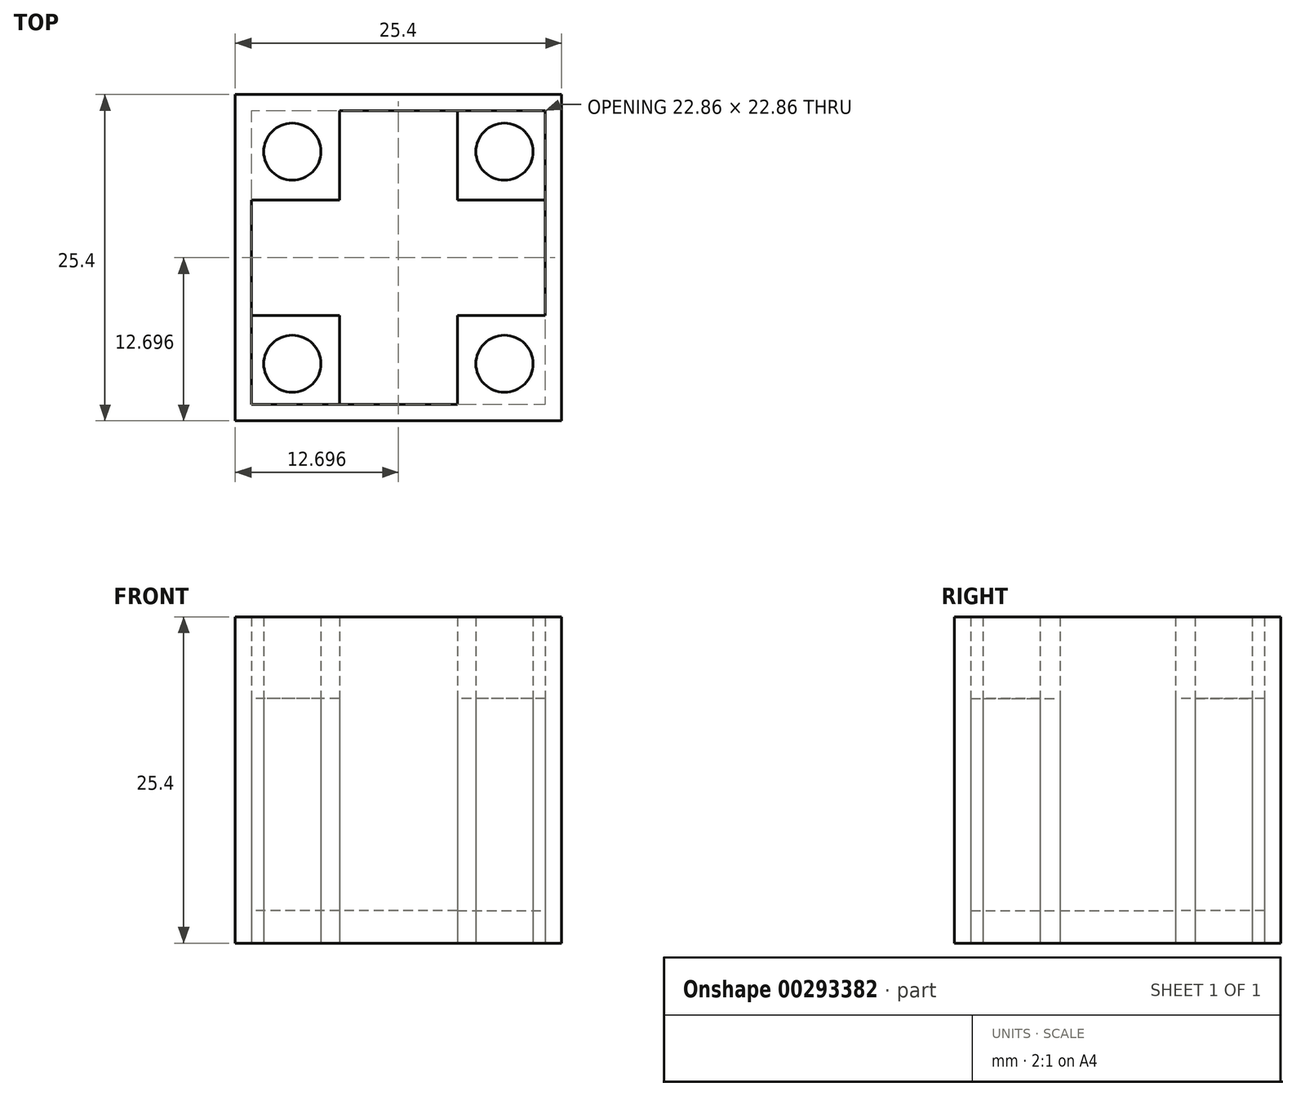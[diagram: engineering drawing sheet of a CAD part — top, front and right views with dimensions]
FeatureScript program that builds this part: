
annotation { "Feature Type Name" : "Feature", "Feature Type Description" : "" }
export const myFeature = defineFeature(function(context is Context, id is Id, definition is map)
    precondition{}
    {
        {
            var Q0;
            Q0=qCreatedBy(makeId("Top.planeOp"),FACE);
            var sketch = newSketch(context, id + "F0", { "sketchPlane" : qUnion([Q0])});
            skLineSegment(sketch, "E0.bottom", {"start": v(-7.95, 16.08) * mm, "end": v(17.45, 16.08) * mm});
            skLineSegment(sketch, "E0.top", {"start": v(-7.95, -9.32) * mm, "end": v(17.45, -9.32) * mm});
            skLineSegment(sketch, "E0.left", {"start": v(-7.95, 16.08) * mm, "end": v(-7.95, -9.32) * mm});
            skLineSegment(sketch, "E0.right", {"start": v(17.45, 16.08) * mm, "end": v(17.45, -9.32) * mm});
            skLineSegment(sketch, "E1", {"start": v(16.18, 14.8) * mm, "end": v(16.18, -8.05) * mm});
            skLineSegment(sketch, "E2", {"start": v(16.18, -8.05) * mm, "end": v(-6.68, -8.05) * mm});
            skLineSegment(sketch, "E3", {"start": v(-6.68, -8.05) * mm, "end": v(-6.68, 14.8) * mm});
            skLineSegment(sketch, "E4", {"start": v(-6.68, 14.8) * mm, "end": v(-4.14, 14.8) * mm});
            skLineSegment(sketch, "E5", {"start": v(-6.68, -8.05) * mm, "end": v(-4.14, -8.05) * mm});
            skLineSegment(sketch, "E6", {"start": v(16.18, 14.8) * mm, "end": v(13.64, 14.8) * mm});
            skPoint(sketch, "E7.endSnap0", {"position": v(4.75, -9.32) * mm});
            skLineSegment(sketch, "E8", {"start": v(-6.68, 14.8) * mm, "end": v(16.18, 14.8) * mm});
            skPoint(sketch, "E9.endSnap0", {"position": v(4.75, -8.05) * mm});
            skLineSegment(sketch, "E10", {"start": v(0.16, 14.8) * mm, "end": v(0.16, 7.86) * mm});
            skLineSegment(sketch, "E11", {"start": v(0.16, 7.86) * mm, "end": v(-6.68, 7.86) * mm});
            skCircle(sketch, "E12", {"center": v(-3.5, 11.63) * mm, "radius": 2.22 * mm});
            skCircle(sketch, "E13.MirrorC", {"center": v(13, 11.63) * mm, "radius": 2.22 * mm});
            skCircle(sketch, "E14.MirrorC", {"center": v(13, -4.88) * mm, "radius": 2.22 * mm});
            skCircle(sketch, "E15.MirrorC", {"center": v(-3.5, -4.88) * mm, "radius": 2.22 * mm});
            skPoint(sketch, "E16.endSnap0", {"position": v(-6.68, 3.38) * mm});
            skLineSegment(sketch, "E17.MirrorCS", {"start": v(9.34, 7.86) * mm, "end": v(16.18, 7.86) * mm});
            skLineSegment(sketch, "E18.MirrorCS", {"start": v(9.34, 14.8) * mm, "end": v(9.34, 7.86) * mm});
            skLineSegment(sketch, "E19.MirrorCS", {"start": v(9.34, -1.11) * mm, "end": v(16.18, -1.11) * mm});
            skLineSegment(sketch, "E20.MirrorCS", {"start": v(9.34, -8.05) * mm, "end": v(9.34, -1.11) * mm});
            skLineSegment(sketch, "E21.MirrorCS", {"start": v(0.16, -8.05) * mm, "end": v(0.16, -1.11) * mm});
            skLineSegment(sketch, "E22.MirrorCS", {"start": v(0.16, -1.11) * mm, "end": v(-6.68, -1.11) * mm});
            skSolve(sketch);
        }
        {
            var Q0;
            {var subQ6=sQuery(id+"F0.wireOp",EDGE,"E10");Q0=makeQuery(id+"F0.imprint","IMPRINT",FACE,{"disambiguationData":[TD([[makeQuery(id+"F0.imprint","IMPRINT",EDGE,{"derivedFrom":subQ6}),1.0]])]});}
            extrude(context, id + "F1", {"entities" : qUnion([Q0]), "depth" : 2.54 * mm});
        }
        {
            var Q0;
            Q0=makeQuery(id+"F0.imprint","IMPRINT",FACE,{"disambiguationData":[TD([[makeQuery(id+"F0.imprint","IMPRINT",EDGE,{"derivedFrom":sQuery(id+"F0.wireOp",EDGE,"E12")}),1.0]])]});
            var Q1;
            Q1=makeQuery(id+"F0.imprint","IMPRINT",FACE,{"disambiguationData":[TD([[makeQuery(id+"F0.imprint","IMPRINT",EDGE,{"derivedFrom":sQuery(id+"F0.wireOp",EDGE,"E13.MirrorC")}),-1.0]])]});
            var Q2;
            Q2=makeQuery(id+"F0.imprint","IMPRINT",FACE,{"disambiguationData":[TD([[makeQuery(id+"F0.imprint","IMPRINT",EDGE,{"derivedFrom":sQuery(id+"F0.wireOp",EDGE,"E14.MirrorC")}),1.0]])]});
            var Q3;
            Q3=makeQuery(id+"F0.imprint","IMPRINT",FACE,{"disambiguationData":[TD([[makeQuery(id+"F0.imprint","IMPRINT",EDGE,{"derivedFrom":sQuery(id+"F0.wireOp",EDGE,"E15.MirrorC")}),-1.0]])]});
            extrude(context, id + "F2", {"entities" : qUnion([Q0, Q1, Q2, Q3]), "depth" : 19.05 * mm});
        }
        {
            var Q0;
            Q0=makeQuery(id+"F0.imprint","IMPRINT",FACE,{"disambiguationData":[TD([[makeQuery(id+"F0.imprint","IMPRINT",EDGE,{"derivedFrom":sQuery(id+"F0.wireOp",EDGE,"E0.bottom")}),-1.0]])]});
            var Q1;
            {var subQ0=sQuery(id+"F0.wireOp",EDGE,"E10");Q1=makeQuery(id+"F0.imprint","IMPRINT",FACE,{"disambiguationData":[TD([[makeQuery(id+"F0.imprint","IMPRINT",EDGE,{"derivedFrom":subQ0}),-1.0]])]});}
            var Q2;
            {var subQ0=sQuery(id+"F0.wireOp",EDGE,"E5");Q2=makeQuery(id+"F0.imprint","IMPRINT",FACE,{"disambiguationData":[TD([[makeQuery(id+"F0.imprint","IMPRINT",EDGE,{"derivedFrom":subQ0}),1.0]])]});}
            var Q3;
            Q3=makeQuery(id+"F0.imprint","IMPRINT",FACE,{"disambiguationData":[TD([[makeQuery(id+"F0.imprint","IMPRINT",EDGE,{"derivedFrom":sQuery(id+"F0.wireOp",EDGE,"E14.MirrorC")}),-1.0]])]});
            var Q4;
            Q4=makeQuery(id+"F0.imprint","IMPRINT",FACE,{"disambiguationData":[TD([[makeQuery(id+"F0.imprint","IMPRINT",EDGE,{"derivedFrom":sQuery(id+"F0.wireOp",EDGE,"E13.MirrorC")}),1.0]])]});
            extrude(context, id + "F3", {"entities" : qUnion([Q0, Q1, Q2, Q3, Q4]), "depth" : 25.4 * mm});
        }
    });
